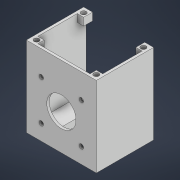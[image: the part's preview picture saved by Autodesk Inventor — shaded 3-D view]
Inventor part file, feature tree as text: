
AUTODESK INVENTOR PART (.ipt)
format: ipt  version: 2021 (Build 250183000, 183)  size: 442,368 bytes
history: native  units: mm
features: extrude x9, sketch x9
ambient origin geometry x8: Origin, YZ Plane, XZ Plane, XY Plane, X Axis, Y Axis, Z Axis, Center Point
bodies: Volumenkörper1 (feature_tree)
feature tree (18):
  extrude  "Extrusion1"  Depth=45.0mm
  extrude  "Extrusion2"  Depth=2.0mm
  extrude  "Extrusion3"  Depth=23.0mm
  extrude  "Extrusion6"  Depth=3.5mm
  extrude  "Extrusion7"  Depth=3.5mm
  extrude  "Extrusion8"  Depth=45.0mm TaperAngle=0.0deg
  sketch  "Skizze13"  dims[d43=2.0mm d44=2.0mm]
  extrude  "Extrusion11"  Depth=2.0mm
  extrude  "Extrusion12"  TaperAngle=0.0deg  [1 undecoded]
  extrude  "Extrusion13"  Depth=6.0mm
  sketch  "Skizze1"  dims[d0=55.0mm d1=45.0mm]
  sketch  "Skizze2"  dims[d2=3.0mm d3=0.0mm d4=2.0mm]
  sketch  "Skizze3"  dims[d5=57.0mm d6=0.0mm d7=23.0mm]
  sketch  "Skizze10"  dims[d10=3.5mm d11=3.5mm]
  sketch  "Skizze11"  dims[d12=3.5mm d13=3.5mm]
  sketch  "Skizze12"  dims[d17=31.5mm d18=45.0mm d19=0.0mm]
  sketch  "Skizze15"  dims[d45=57.0mm d46=0.0mm d48=0.0mm]
  sketch  "Skizze16"  dims[d49=3.0mm d50=0.0mm d52=4.0mm d53=4.0mm d54=4.0mm d55=4.0mm d56=30.0mm d57=30.0mm d58=10.0mm d59=0.0mm d60=5.0mm d61=5.0mm d62=5.0mm d63=5.0mm d64=5.0mm d65=7.0mm d66=5.0mm d67=7.0mm d94=1.5mm d95=4.0mm d96=0.0mm d98=6.0mm d99=0.0mm d100=4.0mm d101=4.0mm d102=4.0mm d103=4.0mm d104=4.0mm d105=4.0mm d106=4.0mm d107=4.0mm d108=4.0mm d109=4.0mm d110=4.0mm d111=4.0mm d112=6.0mm d113=0.0mm d51=0.872665mm]
note: 1 required parameter value undecoded (feature->parameter linkage not recoverable at this tier; creation-order binding heuristic only, values carry confidence <= 0.55)
